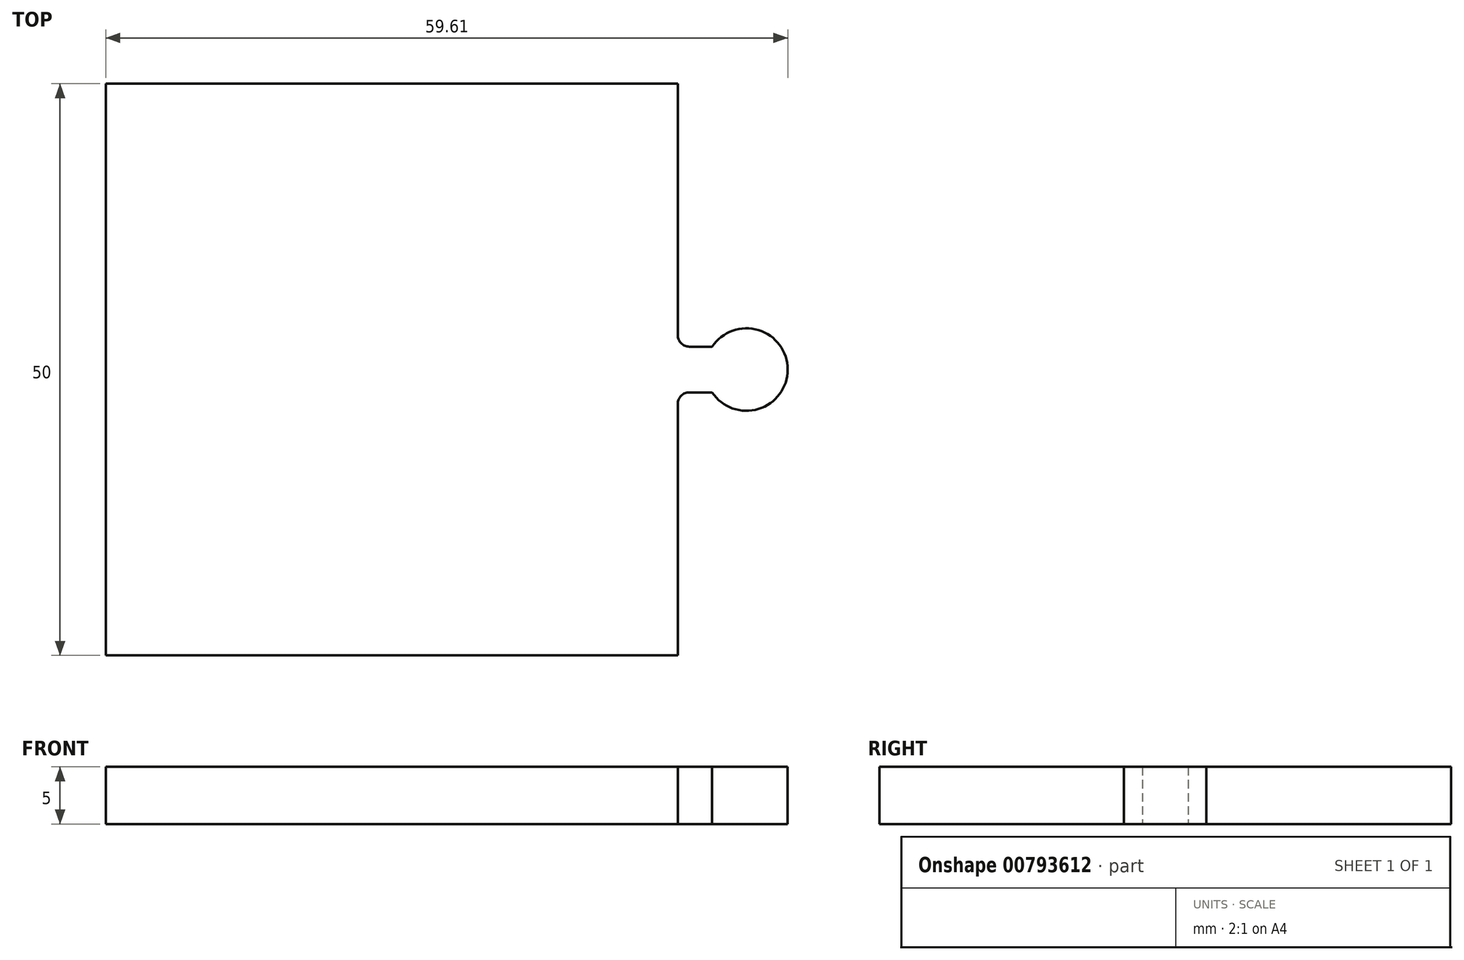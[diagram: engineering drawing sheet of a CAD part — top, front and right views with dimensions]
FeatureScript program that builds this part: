
annotation { "Feature Type Name" : "Feature", "Feature Type Description" : "" }
export const myFeature = defineFeature(function(context is Context, id is Id, definition is map)
    precondition{}
    {
        {
            var Q0;
            Q0=qCreatedBy(makeId("Top.planeOp"),FACE);
            var sketch = newSketch(context, id + "F0", { "sketchPlane" : qUnion([Q0])});
            skLineSegment(sketch, "E0.bottom", {"start": v(25, 25) * mm, "end": v(-25, 25) * mm});
            skLineSegment(sketch, "E0.top", {"start": v(25, -25) * mm, "end": v(-25, -25) * mm});
            skLineSegment(sketch, "E0.left", {"start": v(25, 25) * mm, "end": v(25, 3) * mm});
            skLineSegment(sketch, "E0.right", {"start": v(-25, 25) * mm, "end": v(-25, -25) * mm});
            skPoint(sketch, "E0.middle", {"position": v(0, 0) * mm});
            skLineSegment(sketch, "E1", {"start": v(25, -25) * mm, "end": v(25, -3) * mm});
            skLineSegment(sketch, "E2", {"start": v(26, 2) * mm, "end": v(28, 2) * mm});
            skLineSegment(sketch, "E3", {"start": v(26, -2) * mm, "end": v(28, -2) * mm});
            skArc(sketch, "E4", {"start": v(28, -2) * mm, "mid": v(34.6, 0) * mm, "end": v(28, 2) * mm});
            skLineSegment(sketch, "E5.trimOffspring", {"start": v(25, -3) * mm, "end": v(25, -25) * mm});
            skPoint(sketch, "E6.orphan", {"position": v(25, 0) * mm});
            skArc(sketch, "E7.filletArc", {"start": v(25, 3) * mm, "mid": v(25.3, 2.3) * mm, "end": v(26, 2) * mm});
            skArc(sketch, "E8.filletArc", {"start": v(26, -2) * mm, "mid": v(25.3, -2.3) * mm, "end": v(25, -3) * mm});
            skSolve(sketch);
        }
        {
            var Q0;
            Q0 = qSketchRegion(id + "F0", true);
            extrude(context, id + "F1", {"entities" : qUnion([Q0]), "depth" : 5 * mm, "offsetDistance" : 25 * mm});
        }
    });
